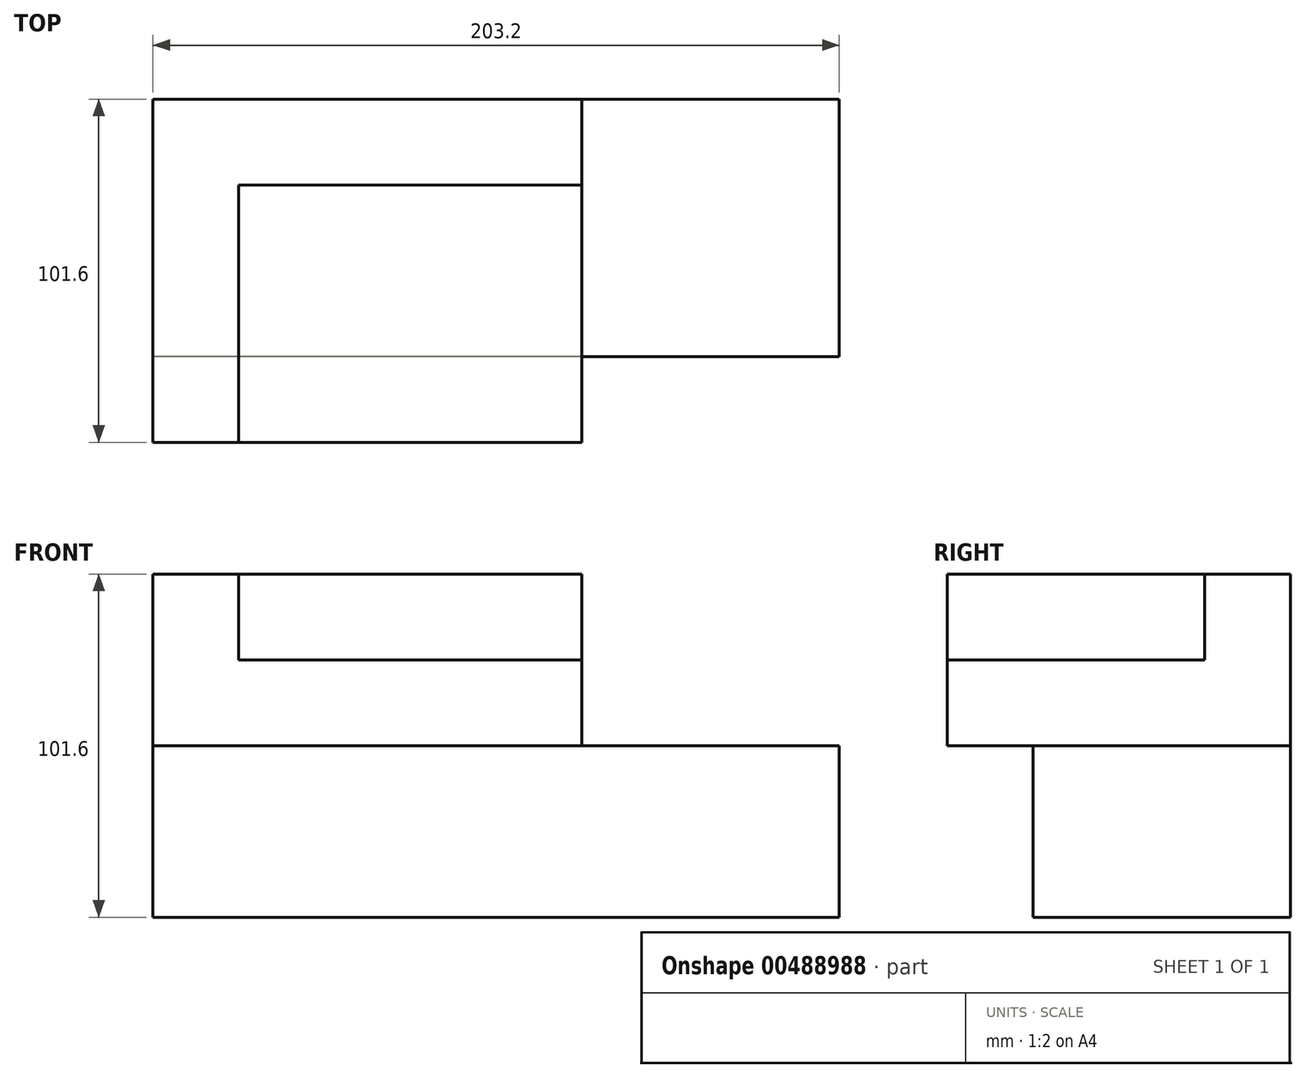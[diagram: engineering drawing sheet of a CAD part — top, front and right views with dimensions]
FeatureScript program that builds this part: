
annotation { "Feature Type Name" : "Feature", "Feature Type Description" : "" }
export const myFeature = defineFeature(function(context is Context, id is Id, definition is map)
    precondition{}
    {
        {
            var Q0;
            Q0=qCreatedBy(makeId("Top.planeOp"),FACE);
            var sketch = newSketch(context, id + "F0", { "sketchPlane" : qUnion([Q0])});
            skLineSegment(sketch, "E0.bottom", {"start": v(115.48, -40.08) * mm, "end": v(-87.72, -40.08) * mm});
            skLineSegment(sketch, "E0.top", {"start": v(115.48, 36.12) * mm, "end": v(-87.72, 36.12) * mm});
            skLineSegment(sketch, "E0.left", {"start": v(115.48, -40.08) * mm, "end": v(115.48, 36.12) * mm});
            skLineSegment(sketch, "E0.right", {"start": v(-87.72, -40.08) * mm, "end": v(-87.72, 36.12) * mm});
            skSolve(sketch);
        }
        {
            var Q0;
            Q0=makeQuery(id+"F0.imprint","IMPRINT",FACE,{"disambiguationData":[TD([[makeQuery(id+"F0.imprint","IMPRINT",EDGE,{"derivedFrom":sQuery(id+"F0.wireOp",EDGE,"E0.bottom")}),-1.0]])]});
            extrude(context, id + "F1", {"entities" : qUnion([Q0]), "depth" : 50.8 * mm});
        }
        {
            var Q0;
            Q0=makeQuery(id+"F1.opExtrude","CAP_FACE",FACE,{"disambiguationData":[OSD([sQuery(id+"F0.wireOp",EDGE,"E0.bottom"),sQuery(id+"F0.wireOp",EDGE,"E0.top"),sQuery(id+"F0.wireOp",EDGE,"E0.left"),sQuery(id+"F0.wireOp",EDGE,"E0.right")])],"isStart":false});
            var sketch = newSketch(context, id + "F2", { "sketchPlane" : qUnion([Q0])});
            skLineSegment(sketch, "E1.bottom", {"start": v(-87.72, 36.12) * mm, "end": v(39.28, 36.12) * mm});
            skLineSegment(sketch, "E1.top", {"start": v(-87.72, -65.48) * mm, "end": v(39.28, -65.48) * mm});
            skLineSegment(sketch, "E1.left", {"start": v(-87.72, 36.12) * mm, "end": v(-87.72, -65.48) * mm});
            skLineSegment(sketch, "E1.right", {"start": v(39.28, 36.12) * mm, "end": v(39.28, -65.48) * mm});
            skSolve(sketch);
        }
        {
            var Q0;
            Q0 = qSketchRegion(id + "F2", true);
            extrude(context, id + "F3", {"entities" : qUnion([Q0]), "operationType" : NewBodyOperationType.ADD, "depth" : 50.8 * mm});
        }
        {
            var Q0;
            Q0=makeQuery(id+"F3.opExtrude","CAP_FACE",FACE,{"disambiguationData":[OSD([sQuery(id+"F2.wireOp",EDGE,"E1.bottom"),sQuery(id+"F2.wireOp",EDGE,"E1.top"),sQuery(id+"F2.wireOp",EDGE,"E1.left"),sQuery(id+"F2.wireOp",EDGE,"E1.right")])],"isStart":false});
            var sketch = newSketch(context, id + "F4", { "sketchPlane" : qUnion([Q0])});
            skLineSegment(sketch, "E2.bottom", {"start": v(39.28, -65.48) * mm, "end": v(-62.32, -65.48) * mm});
            skLineSegment(sketch, "E2.top", {"start": v(39.28, 10.72) * mm, "end": v(-62.32, 10.72) * mm});
            skLineSegment(sketch, "E2.left", {"start": v(39.28, -65.48) * mm, "end": v(39.28, 10.72) * mm});
            skLineSegment(sketch, "E2.right", {"start": v(-62.32, -65.48) * mm, "end": v(-62.32, 10.72) * mm});
            skSolve(sketch);
        }
        {
            var Q0;
            Q0 = qSketchRegion(id + "F4", true);
            extrude(context, id + "F5", {"entities" : qUnion([Q0]), "operationType" : NewBodyOperationType.REMOVE, "oppositeDirection" : true, "depth" : 25.4 * mm});
        }
    });
